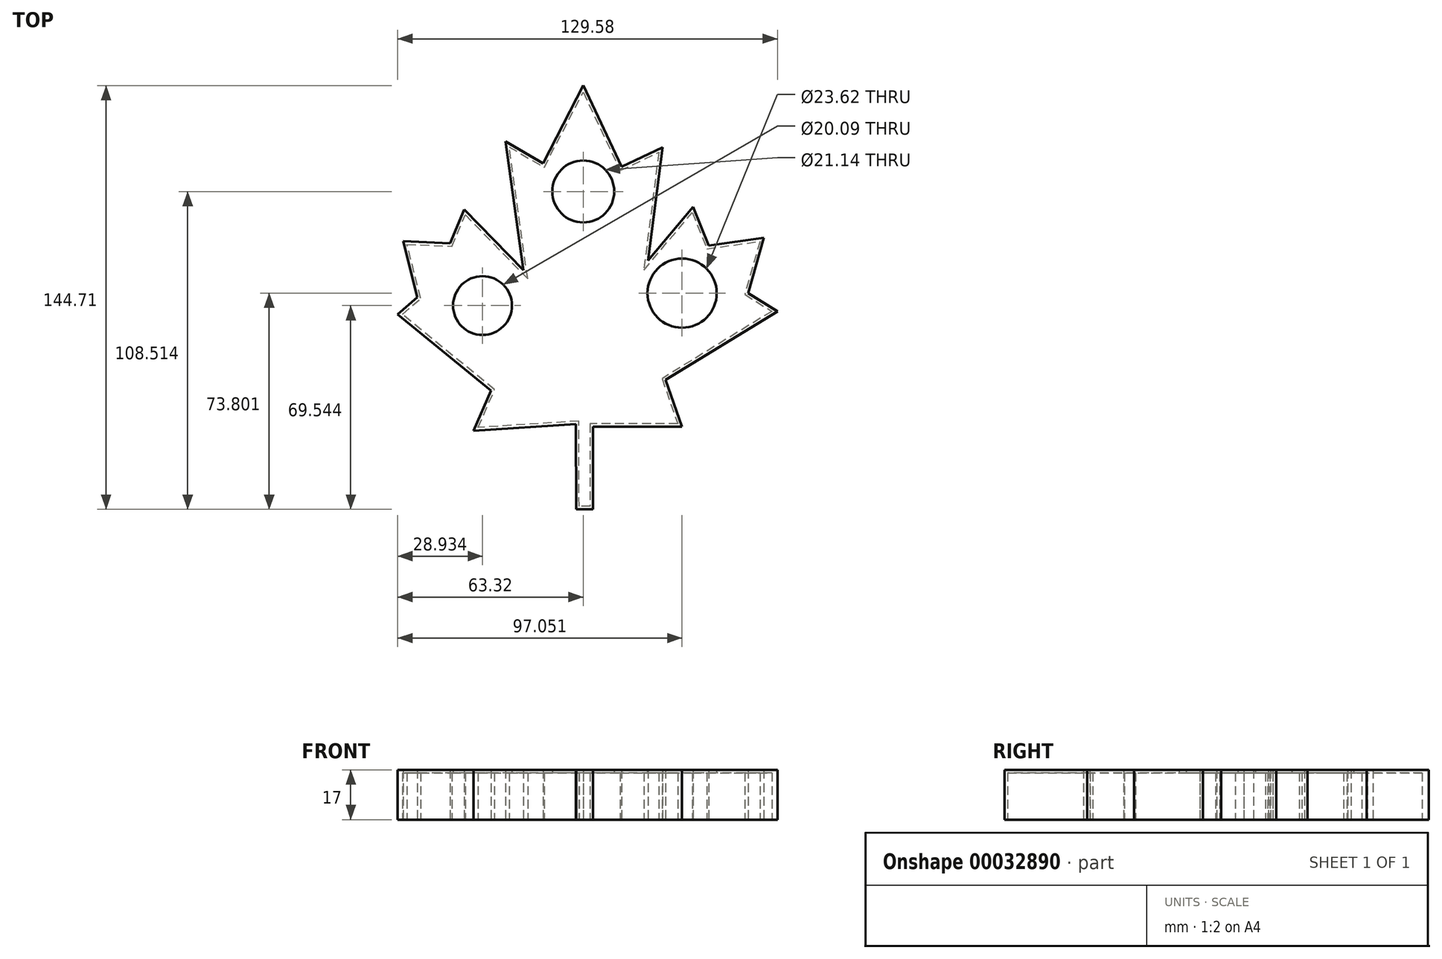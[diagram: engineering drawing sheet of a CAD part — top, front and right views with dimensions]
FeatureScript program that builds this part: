
annotation { "Feature Type Name" : "Feature", "Feature Type Description" : "" }
export const myFeature = defineFeature(function(context is Context, id is Id, definition is map)
    precondition{}
    {
        {
            var Q0;
            Q0=qCreatedBy(makeId("Top.planeOp"),FACE);
            var sketch = newSketch(context, id + "F0", { "sketchPlane" : qUnion([Q0])});
            skLineSegment(sketch, "E0", {"start": v(-2.53, -48.2) * mm, "end": v(-37.47, -50.4) * mm});
            skLineSegment(sketch, "E1", {"start": v(-37.47, -50.4) * mm, "end": v(-31.49, -36.68) * mm});
            skLineSegment(sketch, "E2", {"start": v(-31.49, -36.68) * mm, "end": v(-63.32, -10.65) * mm});
            skLineSegment(sketch, "E3", {"start": v(-63.32, -10.65) * mm, "end": v(-56.57, -4.89) * mm});
            skLineSegment(sketch, "E4", {"start": v(-56.57, -4.89) * mm, "end": v(-61.45, 14.27) * mm});
            skLineSegment(sketch, "E5", {"start": v(-61.45, 14.27) * mm, "end": v(-45.45, 13.57) * mm});
            skLineSegment(sketch, "E6", {"start": v(-45.45, 13.57) * mm, "end": v(-40.6, 25.11) * mm});
            skLineSegment(sketch, "E7", {"start": v(-40.6, 25.11) * mm, "end": v(-20.38, 4.38) * mm});
            skLineSegment(sketch, "E8", {"start": v(-20.38, 4.38) * mm, "end": v(-26.59, 48.4) * mm});
            skLineSegment(sketch, "E9", {"start": v(-26.59, 48.4) * mm, "end": v(-13.74, 40.92) * mm});
            skLineSegment(sketch, "E10", {"start": v(-13.74, 40.92) * mm, "end": v(0, 67.47) * mm});
            skLineSegment(sketch, "E11", {"start": v(0, 67.47) * mm, "end": v(13.1, 39.76) * mm});
            skLineSegment(sketch, "E12", {"start": v(13.1, 39.76) * mm, "end": v(27.01, 46.33) * mm});
            skLineSegment(sketch, "E13", {"start": v(27.01, 46.33) * mm, "end": v(22.08, 7.66) * mm});
            skLineSegment(sketch, "E14", {"start": v(22.08, 7.66) * mm, "end": v(37.54, 26.06) * mm});
            skLineSegment(sketch, "E15", {"start": v(37.54, 26.06) * mm, "end": v(42.84, 12.8) * mm});
            skLineSegment(sketch, "E16", {"start": v(42.84, 12.8) * mm, "end": v(61.67, 15.43) * mm});
            skLineSegment(sketch, "E17", {"start": v(61.67, 15.43) * mm, "end": v(56.27, -3.4) * mm});
            skLineSegment(sketch, "E18", {"start": v(56.27, -3.4) * mm, "end": v(66.26, -9.62) * mm});
            skLineSegment(sketch, "E19", {"start": v(66.26, -9.62) * mm, "end": v(28.1, -33.04) * mm});
            skLineSegment(sketch, "E20", {"start": v(28.1, -33.04) * mm, "end": v(33.67, -49.08) * mm});
            skLineSegment(sketch, "E21", {"start": v(33.67, -49.08) * mm, "end": v(3.35, -49.08) * mm});
            skLineSegment(sketch, "E22", {"start": v(3.35, -49.08) * mm, "end": v(3.35, -77.24) * mm});
            skLineSegment(sketch, "E23", {"start": v(3.35, -77.24) * mm, "end": v(-2.44, -77.24) * mm});
            skLineSegment(sketch, "E24", {"start": v(-2.44, -77.24) * mm, "end": v(-2.53, -48.2) * mm});
            skSolve(sketch);
        }
        {
            var Q0;
            Q0=makeQuery(id+"F0.imprint","IMPRINT",FACE,{"disambiguationData":[TD([[makeQuery(id+"F0.imprint","IMPRINT",EDGE,{"derivedFrom":sQuery(id+"F0.wireOp",EDGE,"E0")}),-1.0]])]});
            extrude(context, id + "F1", {"entities" : qUnion([Q0]), "depth" : 17 * mm});
        }
        {
            var Q0;
            Q0=makeQuery(id+"F1.opExtrude","CAP_FACE",FACE,{"disambiguationData":[OSD([sQuery(id+"F0.wireOp",EDGE,"E0"),sQuery(id+"F0.wireOp",EDGE,"E1"),sQuery(id+"F0.wireOp",EDGE,"E2"),sQuery(id+"F0.wireOp",EDGE,"E3"),sQuery(id+"F0.wireOp",EDGE,"E4"),sQuery(id+"F0.wireOp",EDGE,"E5"),sQuery(id+"F0.wireOp",EDGE,"E6"),sQuery(id+"F0.wireOp",EDGE,"E7"),sQuery(id+"F0.wireOp",EDGE,"E8"),sQuery(id+"F0.wireOp",EDGE,"E9"),sQuery(id+"F0.wireOp",EDGE,"E10"),sQuery(id+"F0.wireOp",EDGE,"E11"),sQuery(id+"F0.wireOp",EDGE,"E12"),sQuery(id+"F0.wireOp",EDGE,"E13"),sQuery(id+"F0.wireOp",EDGE,"E14"),sQuery(id+"F0.wireOp",EDGE,"E15"),sQuery(id+"F0.wireOp",EDGE,"E16"),sQuery(id+"F0.wireOp",EDGE,"E17"),sQuery(id+"F0.wireOp",EDGE,"E18"),sQuery(id+"F0.wireOp",EDGE,"E19"),sQuery(id+"F0.wireOp",EDGE,"E20"),sQuery(id+"F0.wireOp",EDGE,"E21"),sQuery(id+"F0.wireOp",EDGE,"E22"),sQuery(id+"F0.wireOp",EDGE,"E23"),sQuery(id+"F0.wireOp",EDGE,"E24")])],"isStart":true});
            shell(context, id + "F2", {"entities" : qUnion([Q0]), "thickness" : 1 * mm});
        }
        {
            var Q0;
            Q0=makeQuery(id+"F1.opExtrude","CAP_FACE",FACE,{"disambiguationData":[OSD([sQuery(id+"F0.wireOp",EDGE,"E0"),sQuery(id+"F0.wireOp",EDGE,"E1"),sQuery(id+"F0.wireOp",EDGE,"E2"),sQuery(id+"F0.wireOp",EDGE,"E3"),sQuery(id+"F0.wireOp",EDGE,"E4"),sQuery(id+"F0.wireOp",EDGE,"E5"),sQuery(id+"F0.wireOp",EDGE,"E6"),sQuery(id+"F0.wireOp",EDGE,"E7"),sQuery(id+"F0.wireOp",EDGE,"E8"),sQuery(id+"F0.wireOp",EDGE,"E9"),sQuery(id+"F0.wireOp",EDGE,"E10"),sQuery(id+"F0.wireOp",EDGE,"E11"),sQuery(id+"F0.wireOp",EDGE,"E12"),sQuery(id+"F0.wireOp",EDGE,"E13"),sQuery(id+"F0.wireOp",EDGE,"E14"),sQuery(id+"F0.wireOp",EDGE,"E15"),sQuery(id+"F0.wireOp",EDGE,"E16"),sQuery(id+"F0.wireOp",EDGE,"E17"),sQuery(id+"F0.wireOp",EDGE,"E18"),sQuery(id+"F0.wireOp",EDGE,"E19"),sQuery(id+"F0.wireOp",EDGE,"E20"),sQuery(id+"F0.wireOp",EDGE,"E21"),sQuery(id+"F0.wireOp",EDGE,"E22"),sQuery(id+"F0.wireOp",EDGE,"E23"),sQuery(id+"F0.wireOp",EDGE,"E24")])],"isStart":false});
            var sketch = newSketch(context, id + "F3", { "sketchPlane" : qUnion([Q0])});
            skCircle(sketch, "E25", {"center": v(0, -27.56) * mm, "radius": 14.37 * mm});
            skSolve(sketch);
        }
        {
            var Q0;
            Q0=makeQuery(id+"F3.imprint","IMPRINT",FACE,{"disambiguationData":[TD([[makeQuery(id+"F3.imprint","IMPRINT",EDGE,{"derivedFrom":sQuery(id+"F3.wireOp",EDGE,"E25")}),1.0]])]});
            extrude(context, id + "F4", {"entities" : qUnion([Q0]), "operationType" : NewBodyOperationType.REMOVE, "depth" : 25 * mm});
        }
        {
            var Q0;
            Q0=qCreatedBy(makeId("Top.planeOp"),FACE);
            var sketch = newSketch(context, id + "F5", { "sketchPlane" : qUnion([Q0])});
            skCircle(sketch, "E26", {"center": v(0, 31.27) * mm, "radius": 10.57 * mm});
            skCircle(sketch, "E27", {"center": v(-34.39, -7.7) * mm, "radius": 10.05 * mm});
            skCircle(sketch, "E28", {"center": v(33.73, -3.44) * mm, "radius": 11.8 * mm});
            skSolve(sketch);
        }
        {
            var Q0;
            Q0=makeQuery(id+"F5.imprint","IMPRINT",FACE,{"disambiguationData":[TD([[makeQuery(id+"F5.imprint","IMPRINT",EDGE,{"derivedFrom":sQuery(id+"F5.wireOp",EDGE,"E26")}),1.0]])]});
            var Q1;
            Q1=makeQuery(id+"F5.imprint","IMPRINT",FACE,{"disambiguationData":[TD([[makeQuery(id+"F5.imprint","IMPRINT",EDGE,{"derivedFrom":sQuery(id+"F5.wireOp",EDGE,"E27")}),1.0]])]});
            var Q2;
            Q2=makeQuery(id+"F5.imprint","IMPRINT",FACE,{"disambiguationData":[TD([[makeQuery(id+"F5.imprint","IMPRINT",EDGE,{"derivedFrom":sQuery(id+"F5.wireOp",EDGE,"E28")}),1.0]])]});
            extrude(context, id + "F6", {"entities" : qUnion([Q0, Q1, Q2]), "operationType" : NewBodyOperationType.REMOVE, "depth" : 17 * mm});
        }
    });
